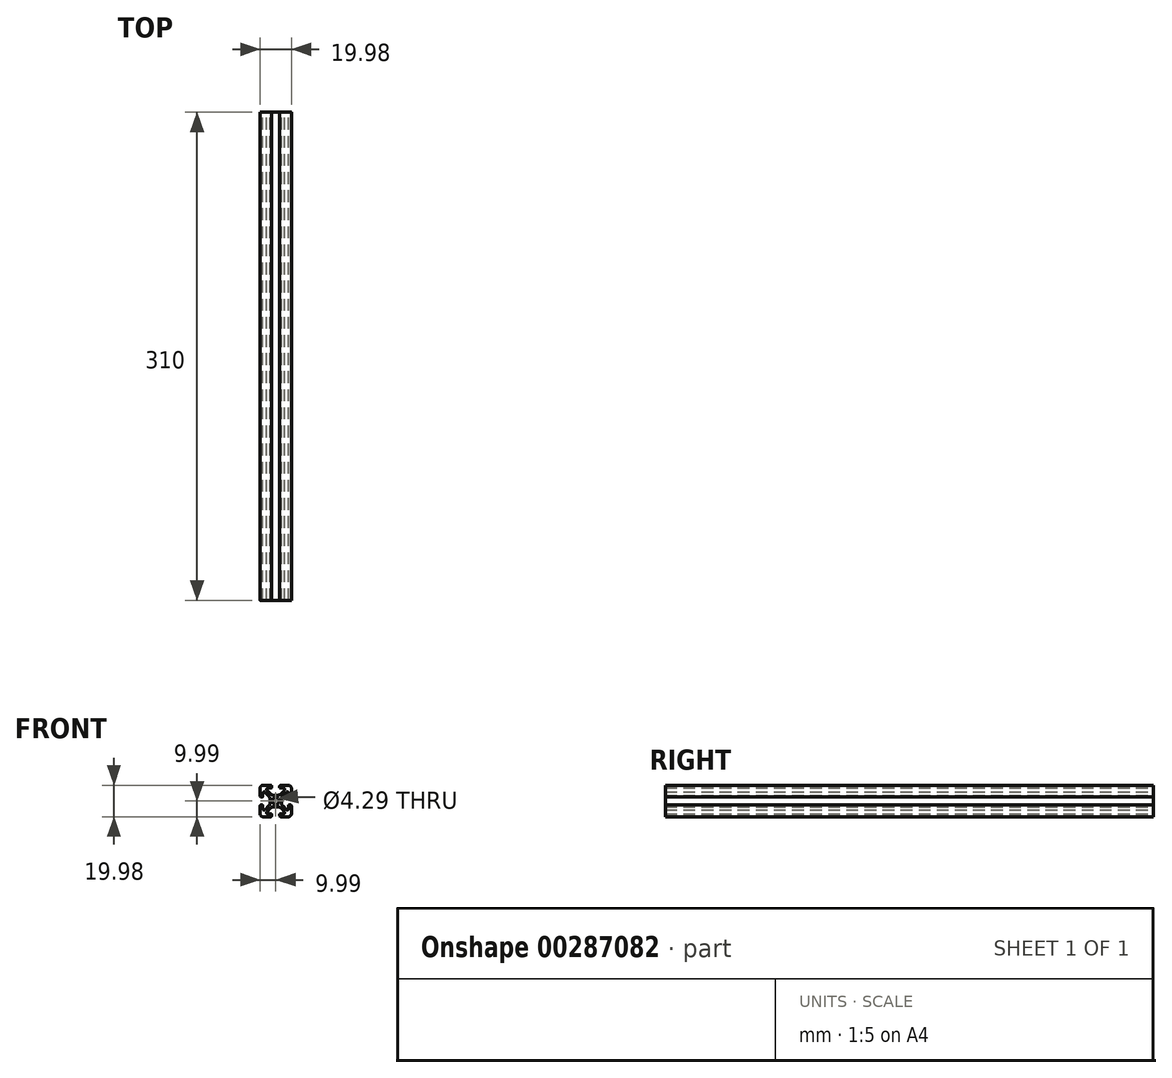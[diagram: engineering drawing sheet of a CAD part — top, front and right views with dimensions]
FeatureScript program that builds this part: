
annotation { "Feature Type Name" : "Feature", "Feature Type Description" : "" }
export const myFeature = defineFeature(function(context is Context, id is Id, definition is map)
    precondition{}
    {
        {
            var Q0;
            Q0=qCreatedBy(makeId("Front.planeOp"),FACE);
            var sketch = newSketch(context, id + "F0", { "sketchPlane" : qUnion([Q0])});
            skLineSegment(sketch, "E0", {"start": v(-7.99, 10) * mm, "end": v(-3.29, 10) * mm});
            skArc(sketch, "E1", {"start": v(-3.29, 10) * mm, "mid": v(-2.73, 9.76) * mm, "end": v(-2.5, 9.2) * mm});
            skLineSegment(sketch, "E2", {"start": v(-2.5, 9.2) * mm, "end": v(-2.5, 8.5) * mm});
            skLineSegment(sketch, "E3", {"start": v(-5.5, 6.76) * mm, "end": v(-3.25, 4.5) * mm});
            skArc(sketch, "E4", {"start": v(-4.91, 8.2) * mm, "mid": v(-5.69, 7.67) * mm, "end": v(-5.5, 6.76) * mm});
            skLineSegment(sketch, "E5", {"start": v(3.29, 10) * mm, "end": v(7.99, 10) * mm});
            skArc(sketch, "E6", {"start": v(2.5, 9.2) * mm, "mid": v(2.73, 9.76) * mm, "end": v(3.29, 10) * mm});
            skLineSegment(sketch, "E7", {"start": v(3.25, 4.5) * mm, "end": v(5.5, 6.76) * mm});
            skArc(sketch, "E8", {"start": v(1.13, 3.63) * mm, "mid": v(2.28, 3.86) * mm, "end": v(3.25, 4.5) * mm});
            skArc(sketch, "E9", {"start": v(7.99, 10) * mm, "mid": v(9.4, 9.4) * mm, "end": v(10, 7.99) * mm});
            skLineSegment(sketch, "E10", {"start": v(-2.8, 8.2) * mm, "end": v(-4.91, 8.2) * mm});
            skArc(sketch, "E11", {"start": v(-2.5, 8.5) * mm, "mid": v(-2.6, 8.28) * mm, "end": v(-2.8, 8.2) * mm});
            skLineSegment(sketch, "E12", {"start": v(4.91, 8.2) * mm, "end": v(2.8, 8.2) * mm});
            skLineSegment(sketch, "E13", {"start": v(2.5, 8.5) * mm, "end": v(2.5, 9.2) * mm});
            skArc(sketch, "E14", {"start": v(2.8, 8.2) * mm, "mid": v(2.6, 8.28) * mm, "end": v(2.5, 8.5) * mm});
            skArc(sketch, "E15", {"start": v(5.5, 6.76) * mm, "mid": v(5.69, 7.67) * mm, "end": v(4.91, 8.2) * mm});
            skLineSegment(sketch, "E16", {"start": v(-1.13, 3.63) * mm, "end": v(1.13, 3.63) * mm});
            skArc(sketch, "E17", {"start": v(-3.25, 4.5) * mm, "mid": v(-2.28, 3.86) * mm, "end": v(-1.13, 3.63) * mm});
            skArc(sketch, "E18", {"start": v(-10, 7.99) * mm, "mid": v(-9.4, 9.4) * mm, "end": v(-7.99, 10) * mm});
            skLineSegment(sketch, "E19", {"start": v(10, 7.99) * mm, "end": v(10, 3.29) * mm});
            skLineSegment(sketch, "E20", {"start": v(4.5, -3.25) * mm, "end": v(6.76, -5.5) * mm});
            skArc(sketch, "E21", {"start": v(3.63, -1.13) * mm, "mid": v(3.86, -2.28) * mm, "end": v(4.5, -3.25) * mm});
            skLineSegment(sketch, "E22", {"start": v(3.63, 1.13) * mm, "end": v(3.63, -1.13) * mm});
            skArc(sketch, "E23", {"start": v(9.2, -2.5) * mm, "mid": v(9.76, -2.73) * mm, "end": v(10, -3.29) * mm});
            skLineSegment(sketch, "E24", {"start": v(10, -3.29) * mm, "end": v(10, -7.99) * mm});
            skLineSegment(sketch, "E25", {"start": v(8.5, -2.5) * mm, "end": v(9.2, -2.5) * mm});
            skLineSegment(sketch, "E26", {"start": v(-9.2, -2.5) * mm, "end": v(-8.5, -2.5) * mm});
            skArc(sketch, "E27", {"start": v(-10, -3.29) * mm, "mid": v(-9.76, -2.73) * mm, "end": v(-9.2, -2.5) * mm});
            skLineSegment(sketch, "E28", {"start": v(-8.2, -2.8) * mm, "end": v(-8.2, -4.91) * mm});
            skLineSegment(sketch, "E29", {"start": v(-10, 3.29) * mm, "end": v(-10, 7.99) * mm});
            skArc(sketch, "E30", {"start": v(-9.2, 2.5) * mm, "mid": v(-9.76, 2.73) * mm, "end": v(-10, 3.29) * mm});
            skLineSegment(sketch, "E31", {"start": v(-4.5, 3.25) * mm, "end": v(-6.76, 5.5) * mm});
            skLineSegment(sketch, "E32", {"start": v(-3.63, -1.13) * mm, "end": v(-3.63, 1.13) * mm});
            skArc(sketch, "E33", {"start": v(-3.63, 1.13) * mm, "mid": v(-3.86, 2.28) * mm, "end": v(-4.5, 3.25) * mm});
            skArc(sketch, "E34", {"start": v(-6.76, 5.5) * mm, "mid": v(-7.67, 5.69) * mm, "end": v(-8.2, 4.91) * mm});
            skLineSegment(sketch, "E35", {"start": v(-8.5, 2.5) * mm, "end": v(-9.2, 2.5) * mm});
            skLineSegment(sketch, "E36", {"start": v(8.2, 2.8) * mm, "end": v(8.2, 4.91) * mm});
            skArc(sketch, "E37", {"start": v(8.2, 4.91) * mm, "mid": v(7.67, 5.69) * mm, "end": v(6.76, 5.5) * mm});
            skLineSegment(sketch, "E38", {"start": v(-10, -7.99) * mm, "end": v(-10, -3.29) * mm});
            skArc(sketch, "E39", {"start": v(-4.5, -3.25) * mm, "mid": v(-3.86, -2.28) * mm, "end": v(-3.63, -1.13) * mm});
            skLineSegment(sketch, "E40", {"start": v(-6.76, -5.5) * mm, "end": v(-4.5, -3.25) * mm});
            skLineSegment(sketch, "E41", {"start": v(1.13, -3.63) * mm, "end": v(-1.13, -3.63) * mm});
            skLineSegment(sketch, "E42", {"start": v(5.5, -6.76) * mm, "end": v(3.25, -4.5) * mm});
            skArc(sketch, "E43", {"start": v(3.25, -4.5) * mm, "mid": v(2.28, -3.86) * mm, "end": v(1.13, -3.63) * mm});
            skLineSegment(sketch, "E44", {"start": v(8.2, -4.91) * mm, "end": v(8.2, -2.8) * mm});
            skLineSegment(sketch, "E45", {"start": v(-4.91, -8.2) * mm, "end": v(-2.8, -8.2) * mm});
            skArc(sketch, "E46", {"start": v(-5.5, -6.76) * mm, "mid": v(-5.69, -7.67) * mm, "end": v(-4.91, -8.2) * mm});
            skArc(sketch, "E47", {"start": v(-8.2, -4.91) * mm, "mid": v(-7.67, -5.69) * mm, "end": v(-6.76, -5.5) * mm});
            skArc(sketch, "E48", {"start": v(-8.5, -2.5) * mm, "mid": v(-8.28, -2.6) * mm, "end": v(-8.2, -2.8) * mm});
            skArc(sketch, "E49", {"start": v(4.91, -8.2) * mm, "mid": v(5.69, -7.67) * mm, "end": v(5.5, -6.76) * mm});
            skLineSegment(sketch, "E50", {"start": v(2.5, -9.2) * mm, "end": v(2.5, -8.5) * mm});
            skArc(sketch, "E51", {"start": v(2.5, -8.5) * mm, "mid": v(2.6, -8.28) * mm, "end": v(2.8, -8.2) * mm});
            skLineSegment(sketch, "E52", {"start": v(2.8, -8.2) * mm, "end": v(4.91, -8.2) * mm});
            skArc(sketch, "E53", {"start": v(3.29, -10) * mm, "mid": v(2.73, -9.76) * mm, "end": v(2.5, -9.2) * mm});
            skArc(sketch, "E54", {"start": v(6.76, -5.5) * mm, "mid": v(7.67, -5.69) * mm, "end": v(8.2, -4.91) * mm});
            skArc(sketch, "E55", {"start": v(10, -7.99) * mm, "mid": v(9.4, -9.4) * mm, "end": v(7.99, -10) * mm});
            skArc(sketch, "E56", {"start": v(4.5, 3.25) * mm, "mid": v(3.86, 2.28) * mm, "end": v(3.63, 1.13) * mm});
            skLineSegment(sketch, "E57", {"start": v(-3.25, -4.5) * mm, "end": v(-5.5, -6.76) * mm});
            skLineSegment(sketch, "E58", {"start": v(-2.5, -8.5) * mm, "end": v(-2.5, -9.2) * mm});
            skArc(sketch, "E59", {"start": v(-2.8, -8.2) * mm, "mid": v(-2.6, -8.28) * mm, "end": v(-2.5, -8.5) * mm});
            skArc(sketch, "E60", {"start": v(-2.5, -9.2) * mm, "mid": v(-2.73, -9.76) * mm, "end": v(-3.29, -10) * mm});
            skArc(sketch, "E61", {"start": v(-1.13, -3.63) * mm, "mid": v(-2.28, -3.86) * mm, "end": v(-3.25, -4.5) * mm});
            skArc(sketch, "E62", {"start": v(10, 3.29) * mm, "mid": v(9.76, 2.73) * mm, "end": v(9.2, 2.5) * mm});
            skLineSegment(sketch, "E63", {"start": v(6.76, 5.5) * mm, "end": v(4.5, 3.25) * mm});
            skLineSegment(sketch, "E64", {"start": v(-8.2, 4.91) * mm, "end": v(-8.2, 2.8) * mm});
            skLineSegment(sketch, "E65", {"start": v(-3.29, -10) * mm, "end": v(-7.99, -10) * mm});
            skArc(sketch, "E66", {"start": v(-7.99, -10) * mm, "mid": v(-9.4, -9.4) * mm, "end": v(-10, -7.99) * mm});
            skLineSegment(sketch, "E67", {"start": v(7.99, -10) * mm, "end": v(3.29, -10) * mm});
            skLineSegment(sketch, "E68", {"start": v(9.2, 2.5) * mm, "end": v(8.5, 2.5) * mm});
            skArc(sketch, "E69", {"start": v(8.5, 2.5) * mm, "mid": v(8.28, 2.6) * mm, "end": v(8.2, 2.8) * mm});
            skCircle(sketch, "E70", {"center": v(0, 0) * mm, "radius": 2.15 * mm});
            skArc(sketch, "E71", {"start": v(-8.2, 2.8) * mm, "mid": v(-8.28, 2.6) * mm, "end": v(-8.5, 2.5) * mm});
            skArc(sketch, "E72", {"start": v(8.2, -2.8) * mm, "mid": v(8.28, -2.6) * mm, "end": v(8.5, -2.5) * mm});
            skSolve(sketch);
        }
        {
            var Q0;
            Q0=qSketchRegion(id+"F0",true);
            extrude(context, id + "F1", {"entities" : qUnion([Q0]), "depth" : 310 * mm});
        }
    });
